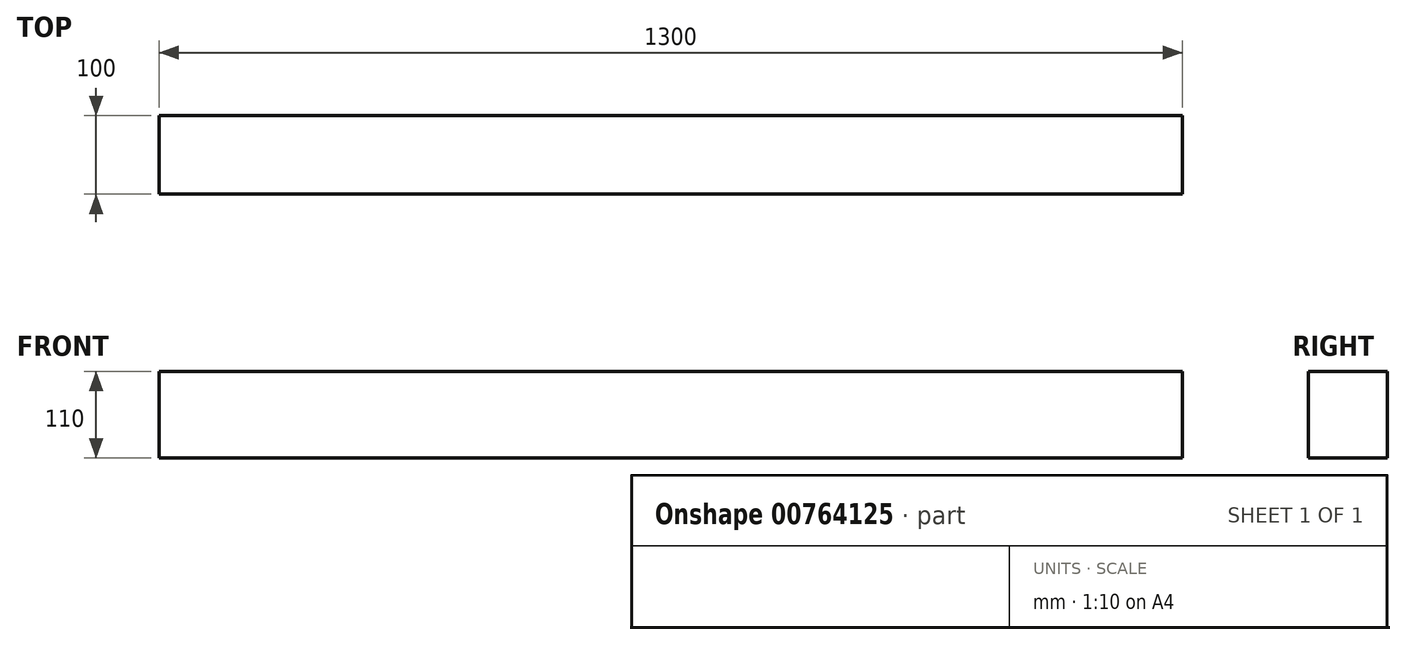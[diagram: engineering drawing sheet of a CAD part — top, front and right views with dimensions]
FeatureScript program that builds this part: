
annotation { "Feature Type Name" : "Feature", "Feature Type Description" : "" }
export const myFeature = defineFeature(function(context is Context, id is Id, definition is map)
    precondition{}
    {
        {
            var Q0;
            Q0=qCreatedBy(makeId("Front.planeOp"),FACE);
            var sketch = newSketch(context, id + "F0", { "sketchPlane" : qUnion([Q0])});
            skLineSegment(sketch, "E0.bottom", {"start": v(0, 0) * mm, "end": v(1300, 0) * mm});
            skLineSegment(sketch, "E0.top", {"start": v(0, 110) * mm, "end": v(1300, 110) * mm});
            skLineSegment(sketch, "E0.left", {"start": v(0, 0) * mm, "end": v(0, 110) * mm});
            skLineSegment(sketch, "E0.right", {"start": v(1300, 0) * mm, "end": v(1300, 110) * mm});
            skSolve(sketch);
        }
        {
            var Q0;
            Q0 = qSketchRegion(id + "F0", true);
            extrude(context, id + "F1", {"entities" : qUnion([Q0]), "oppositeDirection" : true, "depth" : 100 * mm, "offsetDistance" : 25 * mm});
        }
    });
